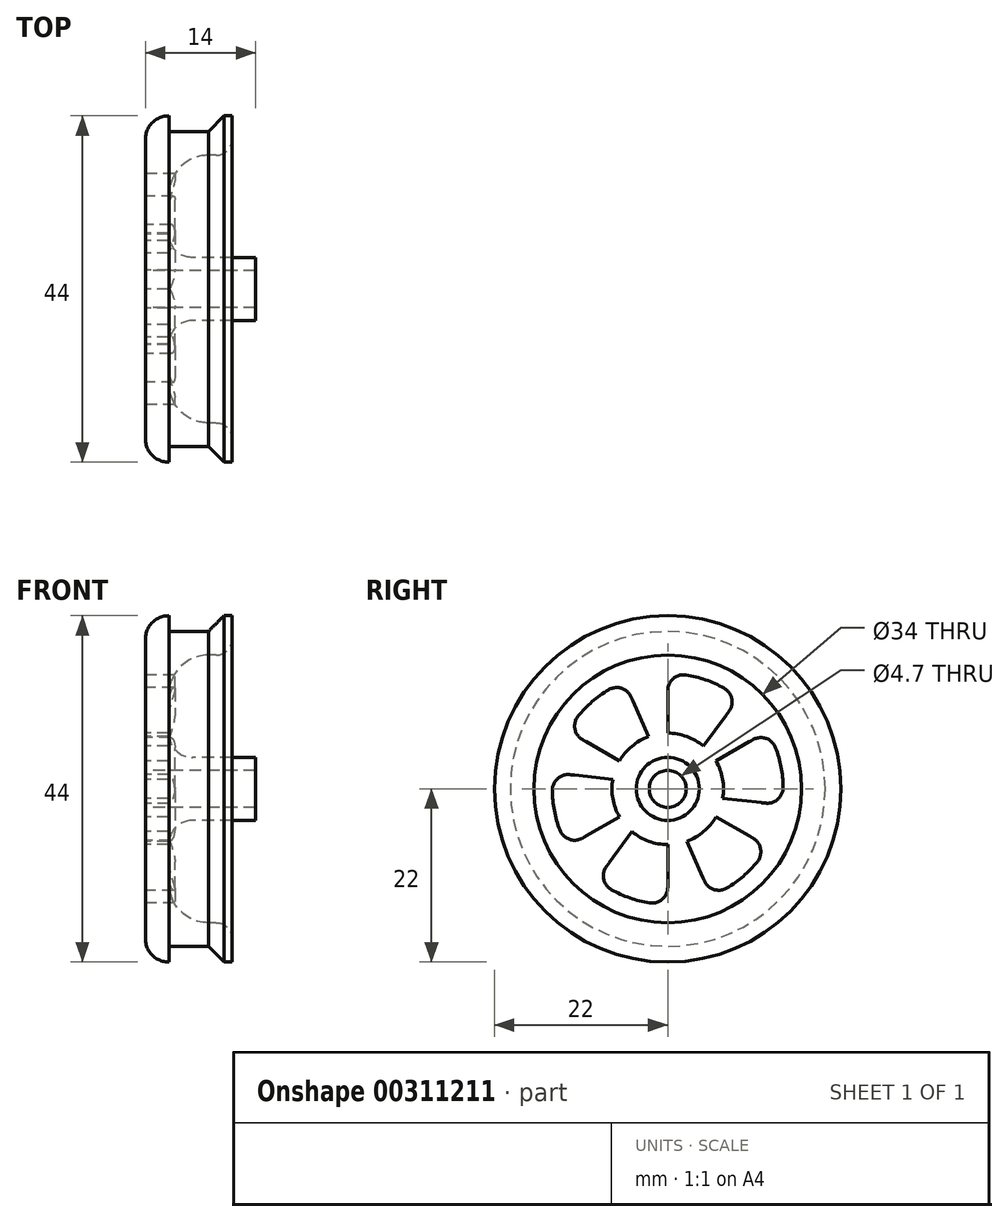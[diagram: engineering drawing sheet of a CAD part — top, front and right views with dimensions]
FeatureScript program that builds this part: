
annotation { "Feature Type Name" : "Feature", "Feature Type Description" : "" }
export const myFeature = defineFeature(function(context is Context, id is Id, definition is map)
    precondition{}
    {
        {
            var Q0;
            Q0=qCreatedBy(makeId("Top.planeOp"),FACE);
            var sketch = newSketch(context, id + "F0", { "sketchPlane" : qUnion([Q0])});
            skLineSegment(sketch, "E0", {"start": v(0, 0) * mm, "end": v(14, 0) * mm});
            skLineSegment(sketch, "E1", {"start": v(14, 0) * mm, "end": v(14, 4) * mm});
            skLineSegment(sketch, "E2", {"start": v(14, 4) * mm, "end": v(3, 4) * mm});
            skLineSegment(sketch, "E3", {"start": v(3, 4) * mm, "end": v(3, 17) * mm});
            skLineSegment(sketch, "E4", {"start": v(3, 17) * mm, "end": v(11, 17) * mm});
            skLineSegment(sketch, "E5", {"start": v(11, 17) * mm, "end": v(11, 22) * mm});
            skLineSegment(sketch, "E6", {"start": v(11, 22) * mm, "end": v(10, 22) * mm});
            skLineSegment(sketch, "E7", {"start": v(3, 20) * mm, "end": v(3, 22) * mm});
            skLineSegment(sketch, "E8", {"start": v(10, 22) * mm, "end": v(8, 20) * mm});
            skLineSegment(sketch, "E9", {"start": v(8, 20) * mm, "end": v(3, 20) * mm});
            skLineSegment(sketch, "E10", {"start": v(0, 0) * mm, "end": v(0, 22) * mm});
            skLineSegment(sketch, "E11", {"start": v(0, 22) * mm, "end": v(3, 22) * mm});
            skLineSegment(sketch, "E12", {"start": v(0, 0) * mm, "end": v(39.24, 0) * mm, "construction": true});
            skSolve(sketch);
        }
        {
            var Q0;
            Q0=makeQuery(id+"F0.imprint","IMPRINT",FACE,{"disambiguationData":[TD([[makeQuery(id+"F0.imprint","IMPRINT",EDGE,{"derivedFrom":sQuery(id+"F0.wireOp",EDGE,"E0")}),1.0]])]});
            var Q1;
            Q1=sQuery(id+"F0.wireOp",EDGE,"E12");
            revolve(context, id + "F1", {"entities" : qUnion([Q0]), "axis" : qUnion([Q1]), "revolveType" : RevolveType.FULL});
        }
        {
            var Q0;
            Q0=qCreatedBy(makeId("Right.planeOp"),FACE);
            var sketch = newSketch(context, id + "F2", { "sketchPlane" : qUnion([Q0])});
            skCircle(sketch, "E13", {"center": v(0, 0) * mm, "radius": 2.35 * mm});
            skSolve(sketch);
        }
        {
            var Q0;
            Q0=makeQuery(id+"F2.imprint","IMPRINT",FACE,{"disambiguationData":[TD([[makeQuery(id+"F2.imprint","IMPRINT",EDGE,{"derivedFrom":sQuery(id+"F2.wireOp",EDGE,"E13")}),1.0]])]});
            extrude(context, id + "F3", {"entities" : qUnion([Q0]), "operationType" : NewBodyOperationType.REMOVE, "depth" : 25 * mm});
        }
        {
            var Q0;
            Q0=makeQuery(id+"F1.opRevolve","SWEPT_EDGE",EDGE,{"disambiguationData":[OSD([sQuery(id+"F0.wireOp",EDGE,"E2"),sQuery(id+"F0.wireOp",EDGE,"E3")])]});
            fillet(context, id + "F4", {"entities" : qUnion([Q0]), "radius" : 3 * mm, "tangentPropagation" : true, "allowEdgeOverflow" : false});
        }
        {
            var Q0;
            Q0=makeQuery(id+"F1.opRevolve","SWEPT_EDGE",EDGE,{"disambiguationData":[OSD([sQuery(id+"F0.wireOp",EDGE,"E3"),sQuery(id+"F0.wireOp",EDGE,"E4")])]});
            fillet(context, id + "F5", {"entities" : qUnion([Q0]), "radius" : 5 * mm, "tangentPropagation" : true, "allowEdgeOverflow" : false});
        }
        {
            var Q0;
            Q0=qCreatedBy(makeId("Right.planeOp"),FACE);
            var sketch = newSketch(context, id + "F6", { "sketchPlane" : qUnion([Q0])});
            skArc(sketch, "E14", {"start": v(0, 14.66) * mm, "mid": v(4.77, 13.87) * mm, "end": v(9.03, 11.56) * mm});
            skArc(sketch, "E15", {"start": v(0, 7.08) * mm, "mid": v(2.41, 6.66) * mm, "end": v(4.54, 5.43) * mm});
            skLineSegment(sketch, "E16", {"start": v(0, 7.08) * mm, "end": v(0, 14.66) * mm});
            skLineSegment(sketch, "E17", {"start": v(4.54, 5.43) * mm, "end": v(9.03, 11.56) * mm});
            skLineSegment(sketch, "E18.1.0", {"start": v(-2.44, 6.65) * mm, "end": v(-5.5, 13.6) * mm});
            skLineSegment(sketch, "E18.1.1", {"start": v(-6.13, 3.54) * mm, "end": v(-12.7, 7.33) * mm});
            skArc(sketch, "E18.1.2", {"start": v(-6.13, 3.54) * mm, "mid": v(-4.56, 5.42) * mm, "end": v(-2.44, 6.65) * mm});
            skArc(sketch, "E18.1.3", {"start": v(-12.7, 7.33) * mm, "mid": v(-9.62, 11.07) * mm, "end": v(-5.5, 13.6) * mm});
            skLineSegment(sketch, "E18.2.0", {"start": v(-6.98, 1.21) * mm, "end": v(-14.52, 2.04) * mm});
            skLineSegment(sketch, "E18.2.1", {"start": v(-6.13, -3.54) * mm, "end": v(-12.7, -7.33) * mm});
            skArc(sketch, "E18.2.2", {"start": v(-6.13, -3.54) * mm, "mid": v(-6.97, -1.24) * mm, "end": v(-6.98, 1.21) * mm});
            skArc(sketch, "E18.2.3", {"start": v(-12.7, -7.33) * mm, "mid": v(-14.4, -2.8) * mm, "end": v(-14.52, 2.04) * mm});
            skLineSegment(sketch, "E18.3.0", {"start": v(-4.54, -5.43) * mm, "end": v(-9.03, -11.56) * mm});
            skLineSegment(sketch, "E18.3.1", {"start": v(0, -7.08) * mm, "end": v(0, -14.66) * mm});
            skArc(sketch, "E18.3.2", {"start": v(0, -7.08) * mm, "mid": v(-2.41, -6.66) * mm, "end": v(-4.54, -5.43) * mm});
            skArc(sketch, "E18.3.3", {"start": v(0, -14.66) * mm, "mid": v(-4.77, -13.87) * mm, "end": v(-9.03, -11.56) * mm});
            skLineSegment(sketch, "E18.4.0", {"start": v(2.44, -6.65) * mm, "end": v(5.5, -13.6) * mm});
            skLineSegment(sketch, "E18.4.1", {"start": v(6.13, -3.54) * mm, "end": v(12.7, -7.33) * mm});
            skArc(sketch, "E18.4.2", {"start": v(6.13, -3.54) * mm, "mid": v(4.56, -5.42) * mm, "end": v(2.44, -6.65) * mm});
            skArc(sketch, "E18.4.3", {"start": v(12.7, -7.33) * mm, "mid": v(9.62, -11.07) * mm, "end": v(5.5, -13.6) * mm});
            skLineSegment(sketch, "E19.1.5.0", {"start": v(6.98, -1.21) * mm, "end": v(14.52, -2.04) * mm});
            skLineSegment(sketch, "E19.3.5.0", {"start": v(6.13, 3.54) * mm, "end": v(12.7, 7.33) * mm});
            skArc(sketch, "E19.6.5.0", {"start": v(6.13, 3.54) * mm, "mid": v(6.97, 1.24) * mm, "end": v(6.98, -1.21) * mm});
            skArc(sketch, "E19.10.5.0", {"start": v(12.7, 7.33) * mm, "mid": v(14.4, 2.8) * mm, "end": v(14.52, -2.04) * mm});
            skSolve(sketch);
        }
        {
            var Q0;
            Q0 = qSketchRegion(id + "F6", true);
            extrude(context, id + "F7", {"entities" : qUnion([Q0]), "operationType" : NewBodyOperationType.REMOVE, "depth" : 25 * mm});
        }
        {
            var Q0;
            Q0=makeQuery(id+"F7.boolean.opBoolean","COPY",EDGE,{"derivedFrom":makeQuery(id+"F7.opExtrude","SWEPT_EDGE",EDGE,{"disambiguationData":[OSD([sQuery(id+"F6.wireOp",EDGE,"E18.1.0"),sQuery(id+"F6.wireOp",EDGE,"E18.1.3")])]})});
            fillet(context, id + "F8", {"entities" : qUnion([Q0]), "radius" : 2 * mm, "tangentPropagation" : true, "allowEdgeOverflow" : false});
        }
        {
            var Q0;
            Q0=makeQuery(id+"F7.boolean.opBoolean","COPY",EDGE,{"derivedFrom":makeQuery(id+"F7.opExtrude","SWEPT_EDGE",EDGE,{"disambiguationData":[OSD([sQuery(id+"F6.wireOp",EDGE,"E14"),sQuery(id+"F6.wireOp",EDGE,"E17")])]})});
            var Q1;
            Q1=makeQuery(id+"F7.boolean.opBoolean","COPY",EDGE,{"derivedFrom":makeQuery(id+"F7.opExtrude","SWEPT_EDGE",EDGE,{"disambiguationData":[OSD([sQuery(id+"F6.wireOp",EDGE,"E14"),sQuery(id+"F6.wireOp",EDGE,"E16")])]})});
            var Q2;
            Q2=makeQuery(id+"F7.boolean.opBoolean","COPY",EDGE,{"derivedFrom":makeQuery(id+"F7.opExtrude","SWEPT_EDGE",EDGE,{"disambiguationData":[OSD([sQuery(id+"F6.wireOp",EDGE,"E18.1.1"),sQuery(id+"F6.wireOp",EDGE,"E18.1.3")])]})});
            var Q3;
            Q3=makeQuery(id+"F7.boolean.opBoolean","COPY",EDGE,{"derivedFrom":makeQuery(id+"F7.opExtrude","SWEPT_EDGE",EDGE,{"disambiguationData":[OSD([sQuery(id+"F6.wireOp",EDGE,"E18.4.1"),sQuery(id+"F6.wireOp",EDGE,"E18.4.3")])]})});
            var Q4;
            Q4=makeQuery(id+"F7.boolean.opBoolean","COPY",EDGE,{"derivedFrom":makeQuery(id+"F7.opExtrude","SWEPT_EDGE",EDGE,{"disambiguationData":[OSD([sQuery(id+"F6.wireOp",EDGE,"E18.4.0"),sQuery(id+"F6.wireOp",EDGE,"E18.4.3")])]})});
            var Q5;
            Q5=makeQuery(id+"F7.boolean.opBoolean","COPY",EDGE,{"derivedFrom":makeQuery(id+"F7.opExtrude","SWEPT_EDGE",EDGE,{"disambiguationData":[OSD([sQuery(id+"F6.wireOp",EDGE,"E18.3.0"),sQuery(id+"F6.wireOp",EDGE,"E18.3.3")])]})});
            var Q6;
            Q6=makeQuery(id+"F7.boolean.opBoolean","COPY",EDGE,{"derivedFrom":makeQuery(id+"F7.opExtrude","SWEPT_EDGE",EDGE,{"disambiguationData":[OSD([sQuery(id+"F6.wireOp",EDGE,"E18.3.1"),sQuery(id+"F6.wireOp",EDGE,"E18.3.3")])]})});
            var Q7;
            Q7=makeQuery(id+"F7.boolean.opBoolean","COPY",EDGE,{"derivedFrom":makeQuery(id+"F7.opExtrude","SWEPT_EDGE",EDGE,{"disambiguationData":[OSD([sQuery(id+"F6.wireOp",EDGE,"E18.2.0"),sQuery(id+"F6.wireOp",EDGE,"E18.2.3")])]})});
            var Q8;
            Q8=makeQuery(id+"F7.boolean.opBoolean","COPY",EDGE,{"derivedFrom":makeQuery(id+"F7.opExtrude","SWEPT_EDGE",EDGE,{"disambiguationData":[OSD([sQuery(id+"F6.wireOp",EDGE,"E18.2.1"),sQuery(id+"F6.wireOp",EDGE,"E18.2.3")])]})});
            fillet(context, id + "F9", {"entities" : qUnion([Q0, Q1, Q2, Q3, Q4, Q5, Q6, Q7, Q8]), "radius" : 2 * mm, "tangentPropagation" : true, "allowEdgeOverflow" : false});
        }
        {
            var Q0;
            Q0=makeQuery(id+"F1.opRevolve","SWEPT_EDGE",EDGE,{"disambiguationData":[OSD([sQuery(id+"F0.wireOp",EDGE,"E4"),sQuery(id+"F0.wireOp",EDGE,"E5")])]});
            fillet(context, id + "F10", {"entities" : qUnion([Q0]), "radius" : 2 * mm, "tangentPropagation" : true, "allowEdgeOverflow" : false});
        }
        {
            var Q0;
            Q0=makeQuery(id+"F7.boolean.opBoolean","COPY",EDGE,{"derivedFrom":makeQuery(id+"F7.opExtrude","SWEPT_EDGE",EDGE,{"disambiguationData":[OSD([sQuery(id+"F6.wireOp",EDGE,"E19.3.5.0"),sQuery(id+"F6.wireOp",EDGE,"E19.10.5.0")])]})});
            var Q1;
            Q1=makeQuery(id+"F7.boolean.opBoolean","COPY",EDGE,{"derivedFrom":makeQuery(id+"F7.opExtrude","SWEPT_EDGE",EDGE,{"disambiguationData":[OSD([sQuery(id+"F6.wireOp",EDGE,"E19.1.5.0"),sQuery(id+"F6.wireOp",EDGE,"E19.10.5.0")])]})});
            fillet(context, id + "F11", {"entities" : qUnion([Q0, Q1]), "radius" : 2 * mm, "tangentPropagation" : true, "allowEdgeOverflow" : false});
        }
        {
            var Q0;
            Q0=makeQuery(id+"F1.opRevolve","SWEPT_EDGE",EDGE,{"disambiguationData":[OSD([sQuery(id+"F0.wireOp",EDGE,"E10"),sQuery(id+"F0.wireOp",EDGE,"E11")])]});
            fillet(context, id + "F12", {"entities" : qUnion([Q0]), "radius" : 3 * mm, "tangentPropagation" : true, "allowEdgeOverflow" : false});
        }
    });
